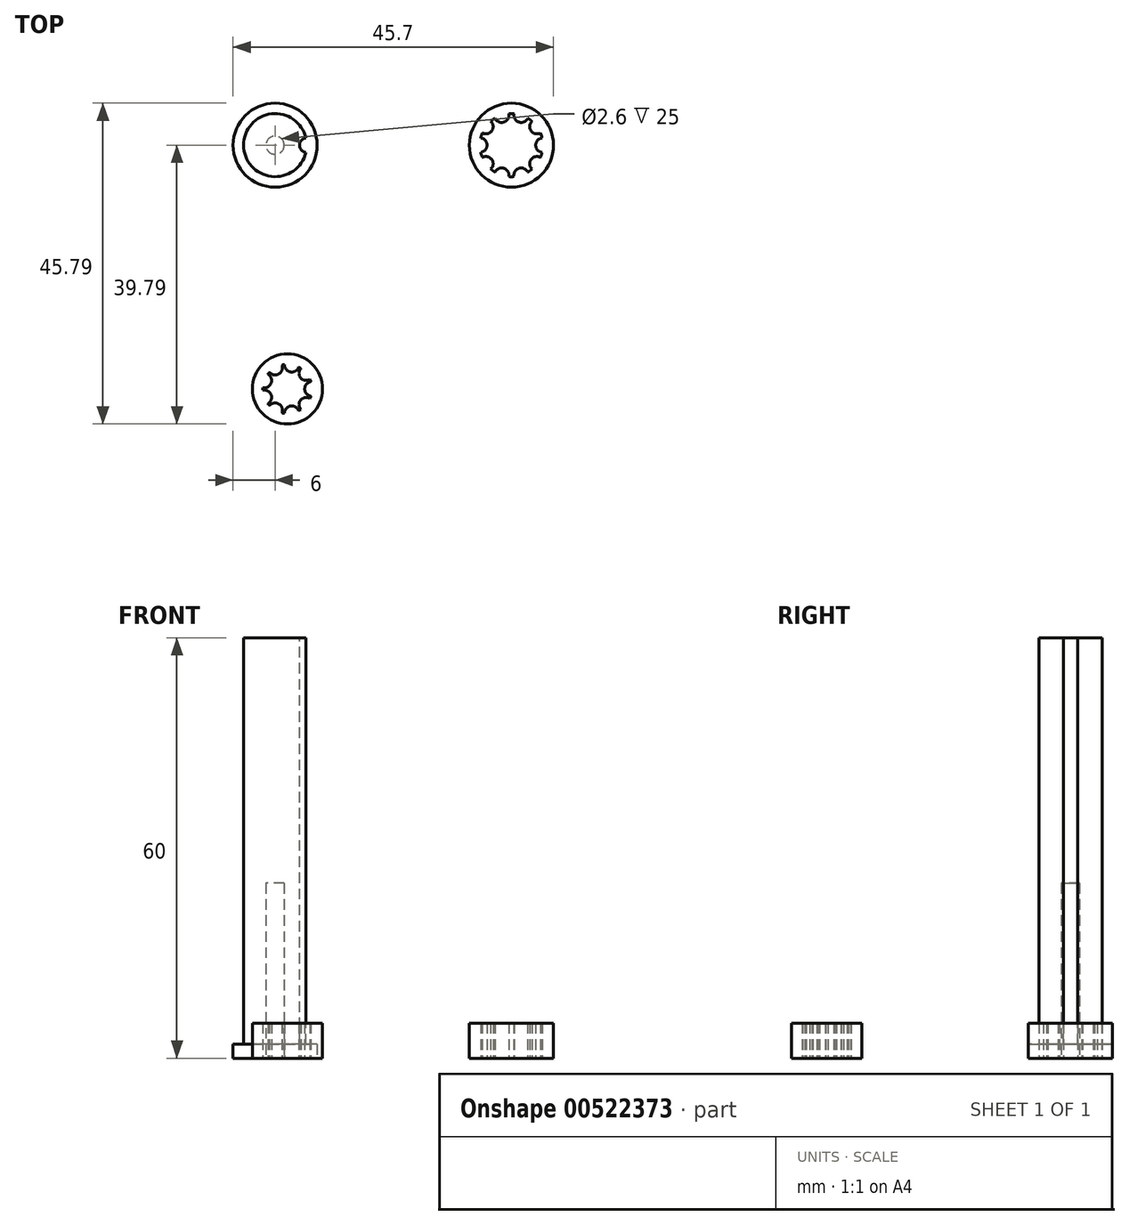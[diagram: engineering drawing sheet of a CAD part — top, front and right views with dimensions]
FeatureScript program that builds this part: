
annotation { "Feature Type Name" : "Feature", "Feature Type Description" : "" }
export const myFeature = defineFeature(function(context is Context, id is Id, definition is map)
    precondition{}
    {
        {
            var Q0;
            Q0=qCreatedBy(makeId("Top.planeOp"),FACE);
            var sketch = newSketch(context, id + "F0", { "sketchPlane" : qUnion([Q0])});
            skCircle(sketch, "E0", {"center": v(0, 0) * mm, "radius": 6 * mm});
            skCircle(sketch, "E1", {"center": v(0, 0) * mm, "radius": 4.5 * mm});
            skSolve(sketch);
        }
        {
            var Q0;
            Q0=makeQuery(id+"F0.imprint","IMPRINT",FACE,{"disambiguationData":[TD([[makeQuery(id+"F0.imprint","IMPRINT",EDGE,{"derivedFrom":sQuery(id+"F0.wireOp",EDGE,"E1")}),1.0]])]});
            extrude(context, id + "F1", {"entities" : qUnion([Q0]), "depth" : 60 * mm, "offsetDistance" : 25 * mm});
        }
        {
            var Q0;
            Q0=makeQuery(id+"F0.imprint","IMPRINT",FACE,{"disambiguationData":[TD([[makeQuery(id+"F0.imprint","IMPRINT",EDGE,{"derivedFrom":sQuery(id+"F0.wireOp",EDGE,"E0")}),1.0]])]});
            extrude(context, id + "F2", {"entities" : qUnion([Q0]), "operationType" : NewBodyOperationType.ADD, "depth" : 2 * mm, "offsetDistance" : 25 * mm});
        }
        {
            var Q0;
            Q0=makeQuery(id+"F1.opExtrude","CAP_FACE",FACE,{"disambiguationData":[OSD([sQuery(id+"F0.wireOp",EDGE,"E1")])],"isStart":false});
            var sketch = newSketch(context, id + "F3", { "sketchPlane" : qUnion([Q0])});
            skCircle(sketch, "E2", {"center": v(4.5, 0) * mm, "radius": 1.03 * mm});
            skSolve(sketch);
        }
        {
            var Q0;
            Q0 = qSketchRegion(id + "F3", true);
            extrude(context, id + "F4", {"entities" : qUnion([Q0]), "operationType" : NewBodyOperationType.REMOVE, "oppositeDirection" : true, "depth" : 58 * mm, "offsetDistance" : 25 * mm});
        }
        {
            var Q0;
            Q0=qCreatedBy(makeId("Front.planeOp"),FACE);
            var sketch = newSketch(context, id + "F5", { "sketchPlane" : qUnion([Q0])});
            skLineSegment(sketch, "E3", {"start": v(0, 0) * mm, "end": v(0, 77.19) * mm, "construction": true});
            skSolve(sketch);
        }
        {
            var Q0;
            Q0=makeQuery(id+"F0.imprint","IMPRINT",FACE,{"disambiguationData":[TD([[makeQuery(id+"F0.imprint","IMPRINT",EDGE,{"derivedFrom":sQuery(id+"F0.wireOp",EDGE,"E1")}),1.0]])]});
            var sketch = newSketch(context, id + "F6", { "sketchPlane" : qUnion([Q0])});
            skCircle(sketch, "E4", {"center": v(0, 0) * mm, "radius": 1.3 * mm});
            skSolve(sketch);
        }
        {
            var Q0;
            Q0 = qSketchRegion(id + "F6", true);
            extrude(context, id + "F7", {"entities" : qUnion([Q0]), "operationType" : NewBodyOperationType.REMOVE, "depth" : 25 * mm, "offsetDistance" : 25 * mm});
        }
        {
            var Q0;
            Q0=qCreatedBy(makeId("Top.planeOp"),FACE);
            var sketch = newSketch(context, id + "F8", { "sketchPlane" : qUnion([Q0])});
            skCircle(sketch, "E5", {"center": v(33.7, 0) * mm, "radius": 6 * mm});
            skCircle(sketch, "E6", {"center": v(33.7, 0) * mm, "radius": 4.5 * mm});
            skCircle(sketch, "E7", {"center": v(38.2, 0) * mm, "radius": 1.03 * mm});
            skCircle(sketch, "E8.1.0", {"center": v(37.34, 2.65) * mm, "radius": 1.03 * mm});
            skCircle(sketch, "E8.2.0", {"center": v(35.1, 4.28) * mm, "radius": 1.03 * mm});
            skCircle(sketch, "E8.3.0", {"center": v(32.31, 4.28) * mm, "radius": 1.03 * mm});
            skCircle(sketch, "E8.4.0", {"center": v(30.06, 2.65) * mm, "radius": 1.03 * mm});
            skCircle(sketch, "E8.5.0", {"center": v(29.2, 0) * mm, "radius": 1.03 * mm});
            skCircle(sketch, "E8.6.0", {"center": v(30.06, -2.65) * mm, "radius": 1.03 * mm});
            skCircle(sketch, "E8.7.0", {"center": v(32.31, -4.28) * mm, "radius": 1.03 * mm});
            skCircle(sketch, "E8.8.0", {"center": v(35.1, -4.28) * mm, "radius": 1.03 * mm});
            skCircle(sketch, "E8.9.0", {"center": v(37.34, -2.65) * mm, "radius": 1.03 * mm});
            skSolve(sketch);
        }
        {
            var Q0;
            {var subQ0=sQuery(id+"F8.wireOp",EDGE,"E8.8.0");var subQ1=sQuery(id+"F8.wireOp",EDGE,"E6");var subQ2=makeQuery(id+"F8.imprint","INTERSECT",VERTEX,{"disambiguationData":[OD(0.0)],"derivedFrom":[subQ1,subQ0]});Q0=makeQuery(id+"F8.imprint","IMPRINT",FACE,{"disambiguationData":[TD([[makeQuery(id+"F8.imprint","IMPRINT",EDGE,{"disambiguationData":[TD([[subQ2,-1.0]])],"derivedFrom":subQ1}),1.0]])]});}
            var Q1;
            {var subQ0=sQuery(id+"F8.wireOp",EDGE,"E8.7.0");var subQ1=sQuery(id+"F8.wireOp",EDGE,"E6");var subQ2=makeQuery(id+"F8.imprint","INTERSECT",VERTEX,{"disambiguationData":[OD(0.0)],"derivedFrom":[subQ1,subQ0]});Q1=makeQuery(id+"F8.imprint","IMPRINT",FACE,{"disambiguationData":[TD([[makeQuery(id+"F8.imprint","IMPRINT",EDGE,{"disambiguationData":[TD([[subQ2,-1.0]])],"derivedFrom":subQ1}),1.0]])]});}
            var Q2;
            {var subQ0=sQuery(id+"F8.wireOp",EDGE,"E8.6.0");var subQ1=sQuery(id+"F8.wireOp",EDGE,"E6");var subQ2=makeQuery(id+"F8.imprint","INTERSECT",VERTEX,{"disambiguationData":[OD(0.0)],"derivedFrom":[subQ1,subQ0]});Q2=makeQuery(id+"F8.imprint","IMPRINT",FACE,{"disambiguationData":[TD([[makeQuery(id+"F8.imprint","IMPRINT",EDGE,{"disambiguationData":[TD([[subQ2,-1.0]])],"derivedFrom":subQ1}),1.0]])]});}
            var Q3;
            Q3=makeQuery(id+"F8.imprint","IMPRINT",FACE,{"disambiguationData":[TD([[makeQuery(id+"F8.imprint","IMPRINT",EDGE,{"derivedFrom":sQuery(id+"F8.wireOp",EDGE,"E5")}),1.0]])]});
            var Q4;
            {var subQ0=sQuery(id+"F8.wireOp",EDGE,"E8.9.0");var subQ1=sQuery(id+"F8.wireOp",EDGE,"E6");var subQ2=makeQuery(id+"F8.imprint","INTERSECT",VERTEX,{"disambiguationData":[OD(0.0)],"derivedFrom":[subQ1,subQ0]});Q4=makeQuery(id+"F8.imprint","IMPRINT",FACE,{"disambiguationData":[TD([[makeQuery(id+"F8.imprint","IMPRINT",EDGE,{"disambiguationData":[TD([[subQ2,-1.0]])],"derivedFrom":subQ1}),1.0]])]});}
            var Q5;
            {var subQ0=sQuery(id+"F8.wireOp",EDGE,"E8.9.0");var subQ1=sQuery(id+"F8.wireOp",EDGE,"E6");var subQ2=makeQuery(id+"F8.imprint","INTERSECT",VERTEX,{"disambiguationData":[OD(0.0)],"derivedFrom":[subQ1,subQ0]});Q5=makeQuery(id+"F8.imprint","IMPRINT",FACE,{"disambiguationData":[TD([[makeQuery(id+"F8.imprint","IMPRINT",EDGE,{"disambiguationData":[TD([[subQ2,-1.0]])],"derivedFrom":subQ1}),-1.0]])]});}
            var Q6;
            {var subQ0=sQuery(id+"F8.wireOp",EDGE,"E8.8.0");var subQ1=sQuery(id+"F8.wireOp",EDGE,"E6");var subQ2=makeQuery(id+"F8.imprint","INTERSECT",VERTEX,{"disambiguationData":[OD(0.0)],"derivedFrom":[subQ1,subQ0]});Q6=makeQuery(id+"F8.imprint","IMPRINT",FACE,{"disambiguationData":[TD([[makeQuery(id+"F8.imprint","IMPRINT",EDGE,{"disambiguationData":[TD([[subQ2,-1.0]])],"derivedFrom":subQ1}),-1.0]])]});}
            var Q7;
            {var subQ0=sQuery(id+"F8.wireOp",EDGE,"E8.7.0");var subQ1=sQuery(id+"F8.wireOp",EDGE,"E6");var subQ2=makeQuery(id+"F8.imprint","INTERSECT",VERTEX,{"disambiguationData":[OD(0.0)],"derivedFrom":[subQ1,subQ0]});Q7=makeQuery(id+"F8.imprint","IMPRINT",FACE,{"disambiguationData":[TD([[makeQuery(id+"F8.imprint","IMPRINT",EDGE,{"disambiguationData":[TD([[subQ2,-1.0]])],"derivedFrom":subQ1}),-1.0]])]});}
            var Q8;
            {var subQ0=sQuery(id+"F8.wireOp",EDGE,"E8.6.0");var subQ1=sQuery(id+"F8.wireOp",EDGE,"E6");var subQ2=makeQuery(id+"F8.imprint","INTERSECT",VERTEX,{"disambiguationData":[OD(0.0)],"derivedFrom":[subQ1,subQ0]});Q8=makeQuery(id+"F8.imprint","IMPRINT",FACE,{"disambiguationData":[TD([[makeQuery(id+"F8.imprint","IMPRINT",EDGE,{"disambiguationData":[TD([[subQ2,-1.0]])],"derivedFrom":subQ1}),-1.0]])]});}
            var Q9;
            {var subQ0=sQuery(id+"F8.wireOp",EDGE,"E8.5.0");var subQ1=sQuery(id+"F8.wireOp",EDGE,"E6");var subQ2=makeQuery(id+"F8.imprint","INTERSECT",VERTEX,{"disambiguationData":[OD(0.0)],"derivedFrom":[subQ1,subQ0]});Q9=makeQuery(id+"F8.imprint","IMPRINT",FACE,{"disambiguationData":[TD([[makeQuery(id+"F8.imprint","IMPRINT",EDGE,{"disambiguationData":[TD([[subQ2,-1.0]])],"derivedFrom":subQ1}),-1.0]])]});}
            var Q10;
            {var subQ0=sQuery(id+"F8.wireOp",EDGE,"E8.5.0");var subQ1=sQuery(id+"F8.wireOp",EDGE,"E6");var subQ2=makeQuery(id+"F8.imprint","INTERSECT",VERTEX,{"disambiguationData":[OD(0.0)],"derivedFrom":[subQ1,subQ0]});Q10=makeQuery(id+"F8.imprint","IMPRINT",FACE,{"disambiguationData":[TD([[makeQuery(id+"F8.imprint","IMPRINT",EDGE,{"disambiguationData":[TD([[subQ2,-1.0]])],"derivedFrom":subQ1}),1.0]])]});}
            var Q11;
            {var subQ0=sQuery(id+"F8.wireOp",EDGE,"E8.4.0");var subQ1=sQuery(id+"F8.wireOp",EDGE,"E6");var subQ2=makeQuery(id+"F8.imprint","INTERSECT",VERTEX,{"disambiguationData":[OD(0.0)],"derivedFrom":[subQ1,subQ0]});Q11=makeQuery(id+"F8.imprint","IMPRINT",FACE,{"disambiguationData":[TD([[makeQuery(id+"F8.imprint","IMPRINT",EDGE,{"disambiguationData":[TD([[subQ2,-1.0]])],"derivedFrom":subQ1}),-1.0]])]});}
            var Q12;
            {var subQ0=sQuery(id+"F8.wireOp",EDGE,"E8.4.0");var subQ1=sQuery(id+"F8.wireOp",EDGE,"E6");var subQ2=makeQuery(id+"F8.imprint","INTERSECT",VERTEX,{"disambiguationData":[OD(0.0)],"derivedFrom":[subQ1,subQ0]});Q12=makeQuery(id+"F8.imprint","IMPRINT",FACE,{"disambiguationData":[TD([[makeQuery(id+"F8.imprint","IMPRINT",EDGE,{"disambiguationData":[TD([[subQ2,-1.0]])],"derivedFrom":subQ1}),1.0]])]});}
            var Q13;
            {var subQ0=sQuery(id+"F8.wireOp",EDGE,"E8.3.0");var subQ1=sQuery(id+"F8.wireOp",EDGE,"E6");var subQ2=makeQuery(id+"F8.imprint","INTERSECT",VERTEX,{"disambiguationData":[OD(0.0)],"derivedFrom":[subQ1,subQ0]});Q13=makeQuery(id+"F8.imprint","IMPRINT",FACE,{"disambiguationData":[TD([[makeQuery(id+"F8.imprint","IMPRINT",EDGE,{"disambiguationData":[TD([[subQ2,-1.0]])],"derivedFrom":subQ1}),1.0]])]});}
            var Q14;
            {var subQ0=sQuery(id+"F8.wireOp",EDGE,"E8.3.0");var subQ1=sQuery(id+"F8.wireOp",EDGE,"E6");var subQ2=makeQuery(id+"F8.imprint","INTERSECT",VERTEX,{"disambiguationData":[OD(0.0)],"derivedFrom":[subQ1,subQ0]});Q14=makeQuery(id+"F8.imprint","IMPRINT",FACE,{"disambiguationData":[TD([[makeQuery(id+"F8.imprint","IMPRINT",EDGE,{"disambiguationData":[TD([[subQ2,-1.0]])],"derivedFrom":subQ1}),-1.0]])]});}
            var Q15;
            {var subQ0=sQuery(id+"F8.wireOp",EDGE,"E8.2.0");var subQ1=sQuery(id+"F8.wireOp",EDGE,"E6");var subQ2=makeQuery(id+"F8.imprint","INTERSECT",VERTEX,{"disambiguationData":[OD(0.0)],"derivedFrom":[subQ1,subQ0]});Q15=makeQuery(id+"F8.imprint","IMPRINT",FACE,{"disambiguationData":[TD([[makeQuery(id+"F8.imprint","IMPRINT",EDGE,{"disambiguationData":[TD([[subQ2,-1.0]])],"derivedFrom":subQ1}),1.0]])]});}
            var Q16;
            {var subQ0=sQuery(id+"F8.wireOp",EDGE,"E8.2.0");var subQ1=sQuery(id+"F8.wireOp",EDGE,"E6");var subQ2=makeQuery(id+"F8.imprint","INTERSECT",VERTEX,{"disambiguationData":[OD(0.0)],"derivedFrom":[subQ1,subQ0]});Q16=makeQuery(id+"F8.imprint","IMPRINT",FACE,{"disambiguationData":[TD([[makeQuery(id+"F8.imprint","IMPRINT",EDGE,{"disambiguationData":[TD([[subQ2,-1.0]])],"derivedFrom":subQ1}),-1.0]])]});}
            var Q17;
            {var subQ0=sQuery(id+"F8.wireOp",EDGE,"E8.1.0");var subQ1=sQuery(id+"F8.wireOp",EDGE,"E6");var subQ2=makeQuery(id+"F8.imprint","INTERSECT",VERTEX,{"disambiguationData":[OD(0.0)],"derivedFrom":[subQ1,subQ0]});Q17=makeQuery(id+"F8.imprint","IMPRINT",FACE,{"disambiguationData":[TD([[makeQuery(id+"F8.imprint","IMPRINT",EDGE,{"disambiguationData":[TD([[subQ2,-1.0]])],"derivedFrom":subQ1}),1.0]])]});}
            var Q18;
            {var subQ0=sQuery(id+"F8.wireOp",EDGE,"E8.1.0");var subQ1=sQuery(id+"F8.wireOp",EDGE,"E6");var subQ2=makeQuery(id+"F8.imprint","INTERSECT",VERTEX,{"disambiguationData":[OD(0.0)],"derivedFrom":[subQ1,subQ0]});Q18=makeQuery(id+"F8.imprint","IMPRINT",FACE,{"disambiguationData":[TD([[makeQuery(id+"F8.imprint","IMPRINT",EDGE,{"disambiguationData":[TD([[subQ2,-1.0]])],"derivedFrom":subQ1}),-1.0]])]});}
            var Q19;
            {var subQ0=sQuery(id+"F8.wireOp",EDGE,"E7");var subQ1=sQuery(id+"F8.wireOp",EDGE,"E6");var subQ2=makeQuery(id+"F8.imprint","INTERSECT",VERTEX,{"disambiguationData":[OD(0.0)],"derivedFrom":[subQ1,subQ0]});Q19=makeQuery(id+"F8.imprint","IMPRINT",FACE,{"disambiguationData":[TD([[makeQuery(id+"F8.imprint","IMPRINT",EDGE,{"disambiguationData":[TD([[subQ2,1.0]])],"derivedFrom":subQ1}),1.0]])]});}
            var Q20;
            {var subQ0=sQuery(id+"F8.wireOp",EDGE,"E7");var subQ1=sQuery(id+"F8.wireOp",EDGE,"E6");var subQ2=makeQuery(id+"F8.imprint","INTERSECT",VERTEX,{"disambiguationData":[OD(0.0)],"derivedFrom":[subQ1,subQ0]});Q20=makeQuery(id+"F8.imprint","IMPRINT",FACE,{"disambiguationData":[TD([[makeQuery(id+"F8.imprint","IMPRINT",EDGE,{"disambiguationData":[TD([[subQ2,1.0]])],"derivedFrom":subQ1}),-1.0]])]});}
            extrude(context, id + "F9", {"entities" : qUnion([Q0, Q1, Q2, Q3, Q4, Q5, Q6, Q7, Q8, Q9, Q10, Q11, Q12, Q13, Q14, Q15, Q16, Q17, Q18, Q19, Q20]), "depth" : 5 * mm, "offsetDistance" : 25 * mm});
        }
        {
            var Q0;
            Q0=qCreatedBy(makeId("Top.planeOp"),FACE);
            var sketch = newSketch(context, id + "F10", { "sketchPlane" : qUnion([Q0])});
            skCircle(sketch, "E9", {"center": v(1.76, -34.79) * mm, "radius": 5 * mm});
            skCircle(sketch, "E10", {"center": v(1.76, -34.79) * mm, "radius": 3.5 * mm});
            skCircle(sketch, "E11", {"center": v(5.26, -34.79) * mm, "radius": 1.03 * mm});
            skCircle(sketch, "E12.1.0", {"center": v(4.44, -32.54) * mm, "radius": 1.03 * mm});
            skCircle(sketch, "E12.2.0", {"center": v(2.36, -31.34) * mm, "radius": 1.03 * mm});
            skCircle(sketch, "E12.3.0", {"center": v(0, -31.75) * mm, "radius": 1.03 * mm});
            skCircle(sketch, "E12.4.0", {"center": v(-1.53, -33.59) * mm, "radius": 1.03 * mm});
            skCircle(sketch, "E12.5.0", {"center": v(-1.53, -35.98) * mm, "radius": 1.03 * mm});
            skCircle(sketch, "E12.6.0", {"center": v(0, -37.82) * mm, "radius": 1.03 * mm});
            skCircle(sketch, "E12.7.0", {"center": v(2.36, -38.23) * mm, "radius": 1.03 * mm});
            skCircle(sketch, "E12.8.0", {"center": v(4.44, -37.04) * mm, "radius": 1.03 * mm});
            skSolve(sketch);
        }
        {
            var Q0;
            {var subQ0=sQuery(id+"F10.wireOp",EDGE,"E12.2.0");var subQ1=sQuery(id+"F10.wireOp",EDGE,"E10");var subQ2=makeQuery(id+"F10.imprint","INTERSECT",VERTEX,{"disambiguationData":[OD(0.0)],"derivedFrom":[subQ1,subQ0]});Q0=makeQuery(id+"F10.imprint","IMPRINT",FACE,{"disambiguationData":[TD([[makeQuery(id+"F10.imprint","IMPRINT",EDGE,{"disambiguationData":[TD([[subQ2,-1.0]])],"derivedFrom":subQ1}),1.0]])]});}
            var Q1;
            {var subQ0=sQuery(id+"F10.wireOp",EDGE,"E12.2.0");var subQ1=sQuery(id+"F10.wireOp",EDGE,"E10");var subQ2=makeQuery(id+"F10.imprint","INTERSECT",VERTEX,{"disambiguationData":[OD(0.0)],"derivedFrom":[subQ1,subQ0]});Q1=makeQuery(id+"F10.imprint","IMPRINT",FACE,{"disambiguationData":[TD([[makeQuery(id+"F10.imprint","IMPRINT",EDGE,{"disambiguationData":[TD([[subQ2,-1.0]])],"derivedFrom":subQ1}),-1.0]])]});}
            var Q2;
            {var subQ0=sQuery(id+"F10.wireOp",EDGE,"E12.1.0");var subQ1=sQuery(id+"F10.wireOp",EDGE,"E10");var subQ2=makeQuery(id+"F10.imprint","INTERSECT",VERTEX,{"disambiguationData":[OD(0.0)],"derivedFrom":[subQ1,subQ0]});Q2=makeQuery(id+"F10.imprint","IMPRINT",FACE,{"disambiguationData":[TD([[makeQuery(id+"F10.imprint","IMPRINT",EDGE,{"disambiguationData":[TD([[subQ2,-1.0]])],"derivedFrom":subQ1}),-1.0]])]});}
            var Q3;
            {var subQ0=sQuery(id+"F10.wireOp",EDGE,"E12.1.0");var subQ1=sQuery(id+"F10.wireOp",EDGE,"E10");var subQ2=makeQuery(id+"F10.imprint","INTERSECT",VERTEX,{"disambiguationData":[OD(0.0)],"derivedFrom":[subQ1,subQ0]});Q3=makeQuery(id+"F10.imprint","IMPRINT",FACE,{"disambiguationData":[TD([[makeQuery(id+"F10.imprint","IMPRINT",EDGE,{"disambiguationData":[TD([[subQ2,-1.0]])],"derivedFrom":subQ1}),1.0]])]});}
            var Q4;
            {var subQ0=sQuery(id+"F10.wireOp",EDGE,"E11");var subQ1=sQuery(id+"F10.wireOp",EDGE,"E10");var subQ2=makeQuery(id+"F10.imprint","INTERSECT",VERTEX,{"disambiguationData":[OD(0.0)],"derivedFrom":[subQ1,subQ0]});Q4=makeQuery(id+"F10.imprint","IMPRINT",FACE,{"disambiguationData":[TD([[makeQuery(id+"F10.imprint","IMPRINT",EDGE,{"disambiguationData":[TD([[subQ2,1.0]])],"derivedFrom":subQ1}),-1.0]])]});}
            var Q5;
            {var subQ0=sQuery(id+"F10.wireOp",EDGE,"E11");var subQ1=sQuery(id+"F10.wireOp",EDGE,"E10");var subQ2=makeQuery(id+"F10.imprint","INTERSECT",VERTEX,{"disambiguationData":[OD(0.0)],"derivedFrom":[subQ1,subQ0]});Q5=makeQuery(id+"F10.imprint","IMPRINT",FACE,{"disambiguationData":[TD([[makeQuery(id+"F10.imprint","IMPRINT",EDGE,{"disambiguationData":[TD([[subQ2,1.0]])],"derivedFrom":subQ1}),1.0]])]});}
            var Q6;
            {var subQ0=sQuery(id+"F10.wireOp",EDGE,"E12.8.0");var subQ1=sQuery(id+"F10.wireOp",EDGE,"E10");var subQ2=makeQuery(id+"F10.imprint","INTERSECT",VERTEX,{"disambiguationData":[OD(0.0)],"derivedFrom":[subQ1,subQ0]});Q6=makeQuery(id+"F10.imprint","IMPRINT",FACE,{"disambiguationData":[TD([[makeQuery(id+"F10.imprint","IMPRINT",EDGE,{"disambiguationData":[TD([[subQ2,-1.0]])],"derivedFrom":subQ1}),-1.0]])]});}
            var Q7;
            {var subQ0=sQuery(id+"F10.wireOp",EDGE,"E12.7.0");var subQ1=sQuery(id+"F10.wireOp",EDGE,"E10");var subQ2=makeQuery(id+"F10.imprint","INTERSECT",VERTEX,{"disambiguationData":[OD(0.0)],"derivedFrom":[subQ1,subQ0]});Q7=makeQuery(id+"F10.imprint","IMPRINT",FACE,{"disambiguationData":[TD([[makeQuery(id+"F10.imprint","IMPRINT",EDGE,{"disambiguationData":[TD([[subQ2,-1.0]])],"derivedFrom":subQ1}),1.0]])]});}
            var Q8;
            {var subQ0=sQuery(id+"F10.wireOp",EDGE,"E12.7.0");var subQ1=sQuery(id+"F10.wireOp",EDGE,"E10");var subQ2=makeQuery(id+"F10.imprint","INTERSECT",VERTEX,{"disambiguationData":[OD(0.0)],"derivedFrom":[subQ1,subQ0]});Q8=makeQuery(id+"F10.imprint","IMPRINT",FACE,{"disambiguationData":[TD([[makeQuery(id+"F10.imprint","IMPRINT",EDGE,{"disambiguationData":[TD([[subQ2,-1.0]])],"derivedFrom":subQ1}),-1.0]])]});}
            var Q9;
            {var subQ0=sQuery(id+"F10.wireOp",EDGE,"E12.6.0");var subQ1=sQuery(id+"F10.wireOp",EDGE,"E10");var subQ2=makeQuery(id+"F10.imprint","INTERSECT",VERTEX,{"disambiguationData":[OD(0.0)],"derivedFrom":[subQ1,subQ0]});Q9=makeQuery(id+"F10.imprint","IMPRINT",FACE,{"disambiguationData":[TD([[makeQuery(id+"F10.imprint","IMPRINT",EDGE,{"disambiguationData":[TD([[subQ2,-1.0]])],"derivedFrom":subQ1}),1.0]])]});}
            var Q10;
            {var subQ0=sQuery(id+"F10.wireOp",EDGE,"E12.6.0");var subQ1=sQuery(id+"F10.wireOp",EDGE,"E10");var subQ2=makeQuery(id+"F10.imprint","INTERSECT",VERTEX,{"disambiguationData":[OD(0.0)],"derivedFrom":[subQ1,subQ0]});Q10=makeQuery(id+"F10.imprint","IMPRINT",FACE,{"disambiguationData":[TD([[makeQuery(id+"F10.imprint","IMPRINT",EDGE,{"disambiguationData":[TD([[subQ2,-1.0]])],"derivedFrom":subQ1}),-1.0]])]});}
            var Q11;
            {var subQ0=sQuery(id+"F10.wireOp",EDGE,"E12.5.0");var subQ1=sQuery(id+"F10.wireOp",EDGE,"E10");var subQ2=makeQuery(id+"F10.imprint","INTERSECT",VERTEX,{"disambiguationData":[OD(0.0)],"derivedFrom":[subQ1,subQ0]});Q11=makeQuery(id+"F10.imprint","IMPRINT",FACE,{"disambiguationData":[TD([[makeQuery(id+"F10.imprint","IMPRINT",EDGE,{"disambiguationData":[TD([[subQ2,-1.0]])],"derivedFrom":subQ1}),1.0]])]});}
            var Q12;
            {var subQ0=sQuery(id+"F10.wireOp",EDGE,"E12.5.0");var subQ1=sQuery(id+"F10.wireOp",EDGE,"E10");var subQ2=makeQuery(id+"F10.imprint","INTERSECT",VERTEX,{"disambiguationData":[OD(0.0)],"derivedFrom":[subQ1,subQ0]});Q12=makeQuery(id+"F10.imprint","IMPRINT",FACE,{"disambiguationData":[TD([[makeQuery(id+"F10.imprint","IMPRINT",EDGE,{"disambiguationData":[TD([[subQ2,-1.0]])],"derivedFrom":subQ1}),-1.0]])]});}
            var Q13;
            {var subQ0=sQuery(id+"F10.wireOp",EDGE,"E12.4.0");var subQ1=sQuery(id+"F10.wireOp",EDGE,"E10");var subQ2=makeQuery(id+"F10.imprint","INTERSECT",VERTEX,{"disambiguationData":[OD(0.0)],"derivedFrom":[subQ1,subQ0]});Q13=makeQuery(id+"F10.imprint","IMPRINT",FACE,{"disambiguationData":[TD([[makeQuery(id+"F10.imprint","IMPRINT",EDGE,{"disambiguationData":[TD([[subQ2,-1.0]])],"derivedFrom":subQ1}),-1.0]])]});}
            var Q14;
            {var subQ0=sQuery(id+"F10.wireOp",EDGE,"E12.4.0");var subQ1=sQuery(id+"F10.wireOp",EDGE,"E10");var subQ2=makeQuery(id+"F10.imprint","INTERSECT",VERTEX,{"disambiguationData":[OD(0.0)],"derivedFrom":[subQ1,subQ0]});Q14=makeQuery(id+"F10.imprint","IMPRINT",FACE,{"disambiguationData":[TD([[makeQuery(id+"F10.imprint","IMPRINT",EDGE,{"disambiguationData":[TD([[subQ2,-1.0]])],"derivedFrom":subQ1}),1.0]])]});}
            var Q15;
            {var subQ0=sQuery(id+"F10.wireOp",EDGE,"E12.3.0");var subQ1=sQuery(id+"F10.wireOp",EDGE,"E10");var subQ2=makeQuery(id+"F10.imprint","INTERSECT",VERTEX,{"disambiguationData":[OD(0.0)],"derivedFrom":[subQ1,subQ0]});Q15=makeQuery(id+"F10.imprint","IMPRINT",FACE,{"disambiguationData":[TD([[makeQuery(id+"F10.imprint","IMPRINT",EDGE,{"disambiguationData":[TD([[subQ2,-1.0]])],"derivedFrom":subQ1}),1.0]])]});}
            var Q16;
            {var subQ0=sQuery(id+"F10.wireOp",EDGE,"E12.3.0");var subQ1=sQuery(id+"F10.wireOp",EDGE,"E10");var subQ2=makeQuery(id+"F10.imprint","INTERSECT",VERTEX,{"disambiguationData":[OD(0.0)],"derivedFrom":[subQ1,subQ0]});Q16=makeQuery(id+"F10.imprint","IMPRINT",FACE,{"disambiguationData":[TD([[makeQuery(id+"F10.imprint","IMPRINT",EDGE,{"disambiguationData":[TD([[subQ2,-1.0]])],"derivedFrom":subQ1}),-1.0]])]});}
            var Q17;
            Q17=makeQuery(id+"F10.imprint","IMPRINT",FACE,{"disambiguationData":[TD([[makeQuery(id+"F10.imprint","IMPRINT",EDGE,{"derivedFrom":sQuery(id+"F10.wireOp",EDGE,"E9")}),1.0]])]});
            var Q18;
            {var subQ0=sQuery(id+"F10.wireOp",EDGE,"E12.8.0");var subQ1=sQuery(id+"F10.wireOp",EDGE,"E10");var subQ2=makeQuery(id+"F10.imprint","INTERSECT",VERTEX,{"disambiguationData":[OD(0.0)],"derivedFrom":[subQ1,subQ0]});Q18=makeQuery(id+"F10.imprint","IMPRINT",FACE,{"disambiguationData":[TD([[makeQuery(id+"F10.imprint","IMPRINT",EDGE,{"disambiguationData":[TD([[subQ2,-1.0]])],"derivedFrom":subQ1}),1.0]])]});}
            extrude(context, id + "F11", {"entities" : qUnion([Q0, Q1, Q2, Q3, Q4, Q5, Q6, Q7, Q8, Q9, Q10, Q11, Q12, Q13, Q14, Q15, Q16, Q17, Q18]), "depth" : 5 * mm, "offsetDistance" : 25 * mm});
        }
    });
